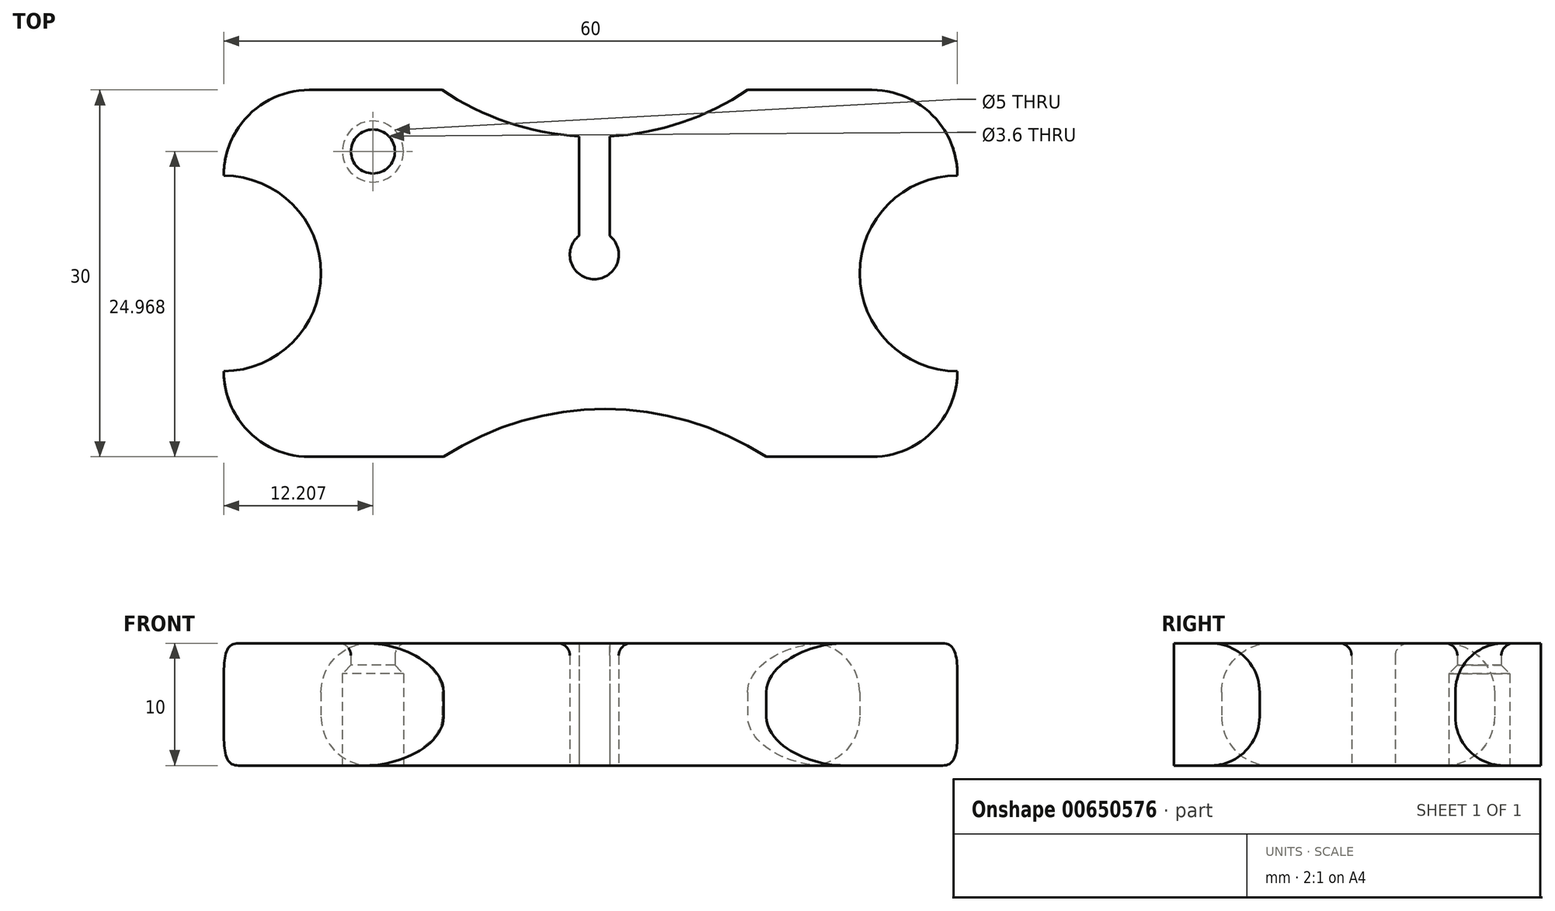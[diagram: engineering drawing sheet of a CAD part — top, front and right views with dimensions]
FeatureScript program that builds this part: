
annotation { "Feature Type Name" : "Feature", "Feature Type Description" : "" }
export const myFeature = defineFeature(function(context is Context, id is Id, definition is map)
    precondition{}
    {
        {
            var Q0;
            Q0=qCreatedBy(makeId("Top.planeOp"),FACE);
            var sketch = newSketch(context, id + "F0", { "sketchPlane" : qUnion([Q0])});
            skLineSegment(sketch, "E0.bottom", {"start": v(-7.03, 19.6) * mm, "end": v(3.84, 19.6) * mm});
            skLineSegment(sketch, "E0.top", {"start": v(-7.03, -10.4) * mm, "end": v(3.96, -10.4) * mm});
            skPoint(sketch, "E1.visualSharp", {"position": v(45.97, 19.6) * mm});
            skArc(sketch, "E1.filletArc", {"start": v(45.97, 12.6) * mm, "mid": v(43.92, 17.55) * mm, "end": v(38.97, 19.6) * mm});
            skPoint(sketch, "E2.visualSharp", {"position": v(45.97, -10.4) * mm});
            skArc(sketch, "E2.filletArc", {"start": v(38.97, -10.4) * mm, "mid": v(43.92, -8.35) * mm, "end": v(45.97, -3.4) * mm});
            skPoint(sketch, "E3.visualSharp", {"position": v(-14.03, -10.4) * mm});
            skArc(sketch, "E3.filletArc", {"start": v(-14.03, -3.4) * mm, "mid": v(-11.98, -8.35) * mm, "end": v(-7.03, -10.4) * mm});
            skPoint(sketch, "E4.visualSharp", {"position": v(-14.03, 19.6) * mm});
            skArc(sketch, "E4.filletArc", {"start": v(-7.03, 19.6) * mm, "mid": v(-11.98, 17.55) * mm, "end": v(-14.03, 12.6) * mm});
            skArc(sketch, "E5", {"start": v(45.97, 12.6) * mm, "mid": v(37.97, 4.6) * mm, "end": v(45.97, -3.4) * mm});
            skArc(sketch, "E6", {"start": v(-14.03, -3.4) * mm, "mid": v(-6.07, 4.6) * mm, "end": v(-14.03, 12.6) * mm});
            skArc(sketch, "E7", {"start": v(3.84, 19.6) * mm, "mid": v(16.32, 15.77) * mm, "end": v(28.81, 19.6) * mm});
            skArc(sketch, "E8", {"start": v(30.35, -10.4) * mm, "mid": v(17.15, -6.5) * mm, "end": v(3.96, -10.4) * mm});
            skLineSegment(sketch, "E9.trimOffspring", {"start": v(30.35, -10.4) * mm, "end": v(38.97, -10.4) * mm});
            skLineSegment(sketch, "E10.trimOffspring", {"start": v(28.81, 19.6) * mm, "end": v(38.97, 19.6) * mm});
            skSolve(sketch);
        }
        {
            var Q0;
            Q0=makeQuery(id+"F0.imprint","IMPRINT",FACE,{"disambiguationData":[TD([[makeQuery(id+"F0.imprint","IMPRINT",EDGE,{"derivedFrom":sQuery(id+"F0.wireOp",EDGE,"E0.bottom")}),-1.0]])]});
            extrude(context, id + "F1", {"entities" : qUnion([Q0]), "depth" : 10 * mm, "offsetDistance" : 25 * mm});
        }
        {
            var Q0;
            Q0=makeQuery(id+"F1.opExtrude","CAP_EDGE",EDGE,{"disambiguationData":[OSD([sQuery(id+"F0.wireOp",EDGE,"E8")])],"isStart":false});
            var Q1;
            Q1=makeQuery(id+"F1.opExtrude","CAP_EDGE",EDGE,{"disambiguationData":[OSD([sQuery(id+"F0.wireOp",EDGE,"E6")])],"isStart":false});
            var Q2;
            Q2=makeQuery(id+"F1.opExtrude","CAP_EDGE",EDGE,{"disambiguationData":[OSD([sQuery(id+"F0.wireOp",EDGE,"E7")])],"isStart":false});
            var Q3;
            Q3=makeQuery(id+"F1.opExtrude","CAP_EDGE",EDGE,{"disambiguationData":[OSD([sQuery(id+"F0.wireOp",EDGE,"E5")])],"isStart":false});
            var Q4;
            Q4=makeQuery(id+"F1.opExtrude","CAP_EDGE",EDGE,{"disambiguationData":[OSD([sQuery(id+"F0.wireOp",EDGE,"E6")])],"isStart":true});
            var Q5;
            Q5=makeQuery(id+"F1.opExtrude","CAP_EDGE",EDGE,{"disambiguationData":[OSD([sQuery(id+"F0.wireOp",EDGE,"E8")])],"isStart":true});
            var Q6;
            Q6=makeQuery(id+"F1.opExtrude","CAP_EDGE",EDGE,{"disambiguationData":[OSD([sQuery(id+"F0.wireOp",EDGE,"E7")])],"isStart":true});
            var Q7;
            Q7=makeQuery(id+"F1.opExtrude","CAP_EDGE",EDGE,{"disambiguationData":[OSD([sQuery(id+"F0.wireOp",EDGE,"E5")])],"isStart":true});
            fillet(context, id + "F2", {"entities" : qUnion([Q0, Q1, Q2, Q3, Q4, Q5, Q6, Q7]), "radius" : 4 * mm, "tangentPropagation" : true, "allowEdgeOverflow" : false});
        }
        {
            var Q0;
            Q0=qCreatedBy(makeId("Top.planeOp"),FACE);
            var sketch = newSketch(context, id + "F3", { "sketchPlane" : qUnion([Q0])});
            skCircle(sketch, "E11", {"center": v(-1.82, 14.57) * mm, "radius": 2.5 * mm});
            skSolve(sketch);
        }
        {
            var Q0;
            Q0=makeQuery(id+"F3.imprint","IMPRINT",FACE,{"disambiguationData":[TD([[makeQuery(id+"F3.imprint","IMPRINT",EDGE,{"derivedFrom":sQuery(id+"F3.wireOp",EDGE,"E11")}),1.0]])]});
            extrude(context, id + "F4", {"entities" : qUnion([Q0]), "operationType" : NewBodyOperationType.REMOVE, "depth" : 7.5 * mm, "offsetDistance" : 25 * mm});
        }
        {
            var Q0;
            Q0=qCreatedBy(makeId("Top.planeOp"),FACE);
            var sketch = newSketch(context, id + "F5", { "sketchPlane" : qUnion([Q0])});
            skCircle(sketch, "E12", {"center": v(-1.82, 14.57) * mm, "radius": 1.8 * mm});
            skSolve(sketch);
        }
        {
            var Q0;
            Q0=makeQuery(id+"F5.imprint","IMPRINT",FACE,{"disambiguationData":[TD([[makeQuery(id+"F5.imprint","IMPRINT",EDGE,{"derivedFrom":sQuery(id+"F5.wireOp",EDGE,"E12")}),1.0]])]});
            extrude(context, id + "F6", {"entities" : qUnion([Q0]), "operationType" : NewBodyOperationType.REMOVE, "depth" : 29.01 * mm, "offsetDistance" : 25 * mm});
        }
        {
            var Q0;
            Q0=makeQuery(id+"F4.boolean.opBoolean","COPY",EDGE,{"derivedFrom":makeQuery(id+"F4.opExtrude","CAP_EDGE",EDGE,{"disambiguationData":[OSD([sQuery(id+"F3.wireOp",EDGE,"E11")])],"isStart":true})});
            var Q1;
            Q1=makeQuery(id+"F6.boolean.opBoolean","INTERSECT",EDGE,{"derivedFrom":[makeQuery(id+"F1.opExtrude","CAP_FACE",FACE,{"disambiguationData":[OSD([sQuery(id+"F0.wireOp",EDGE,"E0.bottom"),sQuery(id+"F0.wireOp",EDGE,"E0.top"),sQuery(id+"F0.wireOp",EDGE,"E1.filletArc"),sQuery(id+"F0.wireOp",EDGE,"E2.filletArc"),sQuery(id+"F0.wireOp",EDGE,"E3.filletArc"),sQuery(id+"F0.wireOp",EDGE,"E4.filletArc"),sQuery(id+"F0.wireOp",EDGE,"E5"),sQuery(id+"F0.wireOp",EDGE,"E6"),sQuery(id+"F0.wireOp",EDGE,"E7"),sQuery(id+"F0.wireOp",EDGE,"E8"),sQuery(id+"F0.wireOp",EDGE,"E9.trimOffspring"),sQuery(id+"F0.wireOp",EDGE,"E10.trimOffspring")])],"isStart":false}),makeQuery(id+"F6.opExtrude","SWEPT_FACE",FACE,{"disambiguationData":[OSD([sQuery(id+"F5.wireOp",EDGE,"E12")])]})]});
            fillet(context, id + "F7", {"entities" : qUnion([Q0, Q1]), "radius" : 1 * mm, "tangentPropagation" : true, "allowEdgeOverflow" : false});
        }
        {
            var Q0;
            Q0=makeQuery(id+"F6.boolean.opBoolean","INTERSECT",EDGE,{"derivedFrom":[makeQuery(id+"F4.boolean.opBoolean","COPY",FACE,{"derivedFrom":makeQuery(id+"F4.opExtrude","CAP_FACE",FACE,{"disambiguationData":[OSD([sQuery(id+"F3.wireOp",EDGE,"E11")])],"isStart":false})}),makeQuery(id+"F6.opExtrude","SWEPT_FACE",FACE,{"disambiguationData":[OSD([sQuery(id+"F5.wireOp",EDGE,"E12")])]})]});
            chamfer(context, id + "F8", {"entities" : qUnion([Q0]), "width" : .7 * mm, "tangentPropagation" : true});
        }
        {
            var Q0;
            Q0=qCreatedBy(makeId("Top.planeOp"),FACE);
            var sketch = newSketch(context, id + "F9", { "sketchPlane" : qUnion([Q0])});
            skLineSegment(sketch, "E13.bottom", {"start": v(15.03, 16.12) * mm, "end": v(17.53, 16.12) * mm});
            skLineSegment(sketch, "E13.left", {"start": v(15.03, 16.12) * mm, "end": v(15.03, 7.68) * mm});
            skLineSegment(sketch, "E13.right", {"start": v(17.53, 16.12) * mm, "end": v(17.53, 7.68) * mm});
            skArc(sketch, "E14", {"start": v(15.03, 7.68) * mm, "mid": v(16.28, 4.12) * mm, "end": v(17.53, 7.68) * mm});
            skPoint(sketch, "E15.orphan", {"position": v(17.53, 6.12) * mm});
            skPoint(sketch, "E16.orphan", {"position": v(15.03, 6.12) * mm});
            skSolve(sketch);
        }
        {
            var Q0;
            Q0=makeQuery(id+"F9.imprint","IMPRINT",FACE,{"disambiguationData":[TD([[makeQuery(id+"F9.imprint","IMPRINT",EDGE,{"derivedFrom":sQuery(id+"F9.wireOp",EDGE,"E13.bottom")}),-1.0]])]});
            extrude(context, id + "F10", {"entities" : qUnion([Q0]), "operationType" : NewBodyOperationType.REMOVE, "oppositeDirection" : true, "depth" : -25 * mm, "offsetDistance" : 25 * mm});
        }
        {
            var Q0;
            Q0=makeQuery(id+"F10.boolean.opBoolean","INTERSECT",EDGE,{"derivedFrom":[makeQuery(id+"F1.opExtrude","CAP_FACE",FACE,{"disambiguationData":[OSD([sQuery(id+"F0.wireOp",EDGE,"E0.bottom"),sQuery(id+"F0.wireOp",EDGE,"E0.top"),sQuery(id+"F0.wireOp",EDGE,"E1.filletArc"),sQuery(id+"F0.wireOp",EDGE,"E2.filletArc"),sQuery(id+"F0.wireOp",EDGE,"E3.filletArc"),sQuery(id+"F0.wireOp",EDGE,"E4.filletArc"),sQuery(id+"F0.wireOp",EDGE,"E5"),sQuery(id+"F0.wireOp",EDGE,"E6"),sQuery(id+"F0.wireOp",EDGE,"E7"),sQuery(id+"F0.wireOp",EDGE,"E8"),sQuery(id+"F0.wireOp",EDGE,"E9.trimOffspring"),sQuery(id+"F0.wireOp",EDGE,"E10.trimOffspring")])],"isStart":false}),makeQuery(id+"F10.opExtrude","SWEPT_FACE",FACE,{"disambiguationData":[OSD([sQuery(id+"F9.wireOp",EDGE,"E14")])]})]});
            var Q1;
            Q1=makeQuery(id+"F10.boolean.opBoolean","COPY",EDGE,{"derivedFrom":makeQuery(id+"F10.opExtrude","CAP_EDGE",EDGE,{"disambiguationData":[OSD([sQuery(id+"F9.wireOp",EDGE,"E14")])],"isStart":true})});
            fillet(context, id + "F11", {"entities" : qUnion([Q0, Q1]), "radius" : 1 * mm, "tangentPropagation" : true, "allowEdgeOverflow" : false});
        }
    });
